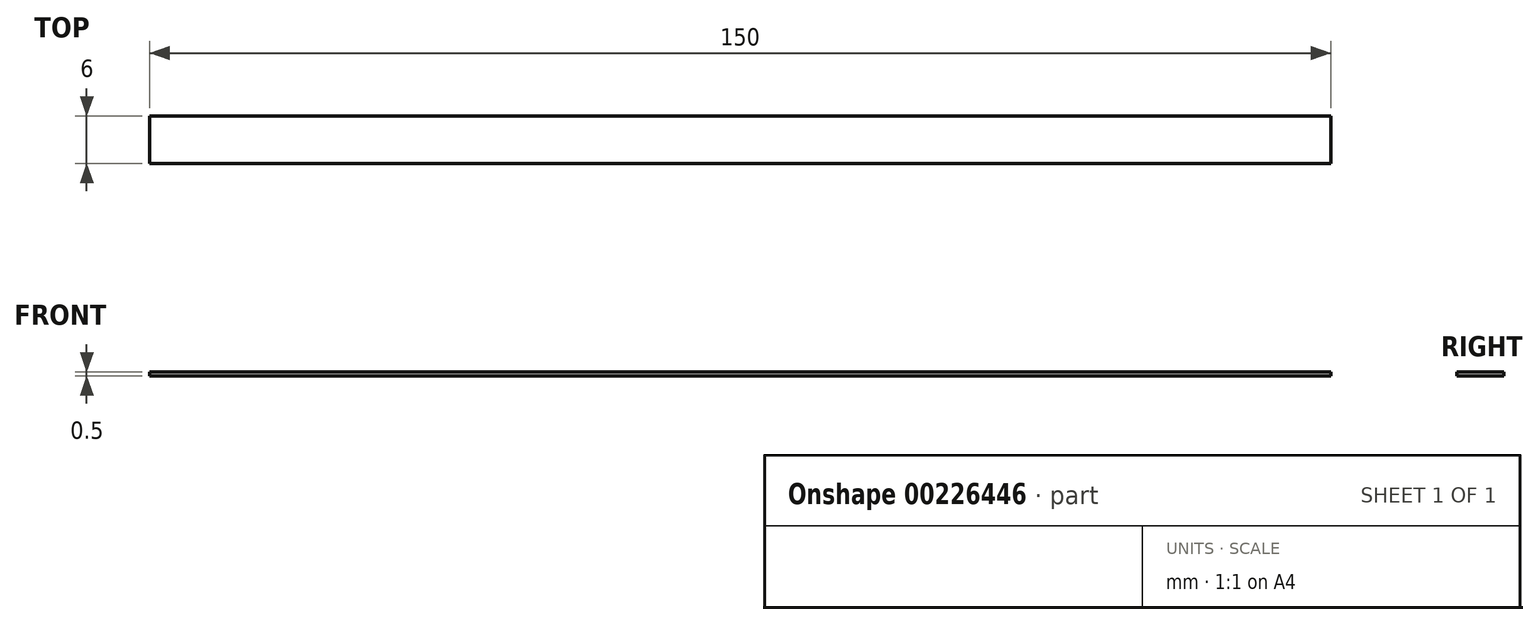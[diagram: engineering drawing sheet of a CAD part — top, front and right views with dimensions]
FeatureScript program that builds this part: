
annotation { "Feature Type Name" : "Feature", "Feature Type Description" : "" }
export const myFeature = defineFeature(function(context is Context, id is Id, definition is map)
    precondition{}
    {
        {
            var Q0;
            Q0=qCreatedBy(makeId("Top.planeOp"),FACE);
            var sketch = newSketch(context, id + "F0", { "sketchPlane" : qUnion([Q0])});
            skLineSegment(sketch, "E0.bottom", {"start": v(75, -3) * mm, "end": v(-75, -3) * mm});
            skLineSegment(sketch, "E0.top", {"start": v(75, 3) * mm, "end": v(-75, 3) * mm});
            skLineSegment(sketch, "E0.left", {"start": v(75, -3) * mm, "end": v(75, 3) * mm});
            skLineSegment(sketch, "E0.right", {"start": v(-75, -3) * mm, "end": v(-75, 3) * mm});
            skPoint(sketch, "E0.middle", {"position": v(0, 0) * mm});
            skSolve(sketch);
        }
        {
            var Q0;
            Q0 = qSketchRegion(id + "F0", true);
            extrude(context, id + "F1", {"entities" : qUnion([Q0]), "depth" : .5 * mm, "offsetDistance" : 25.4 * mm});
        }
    });
